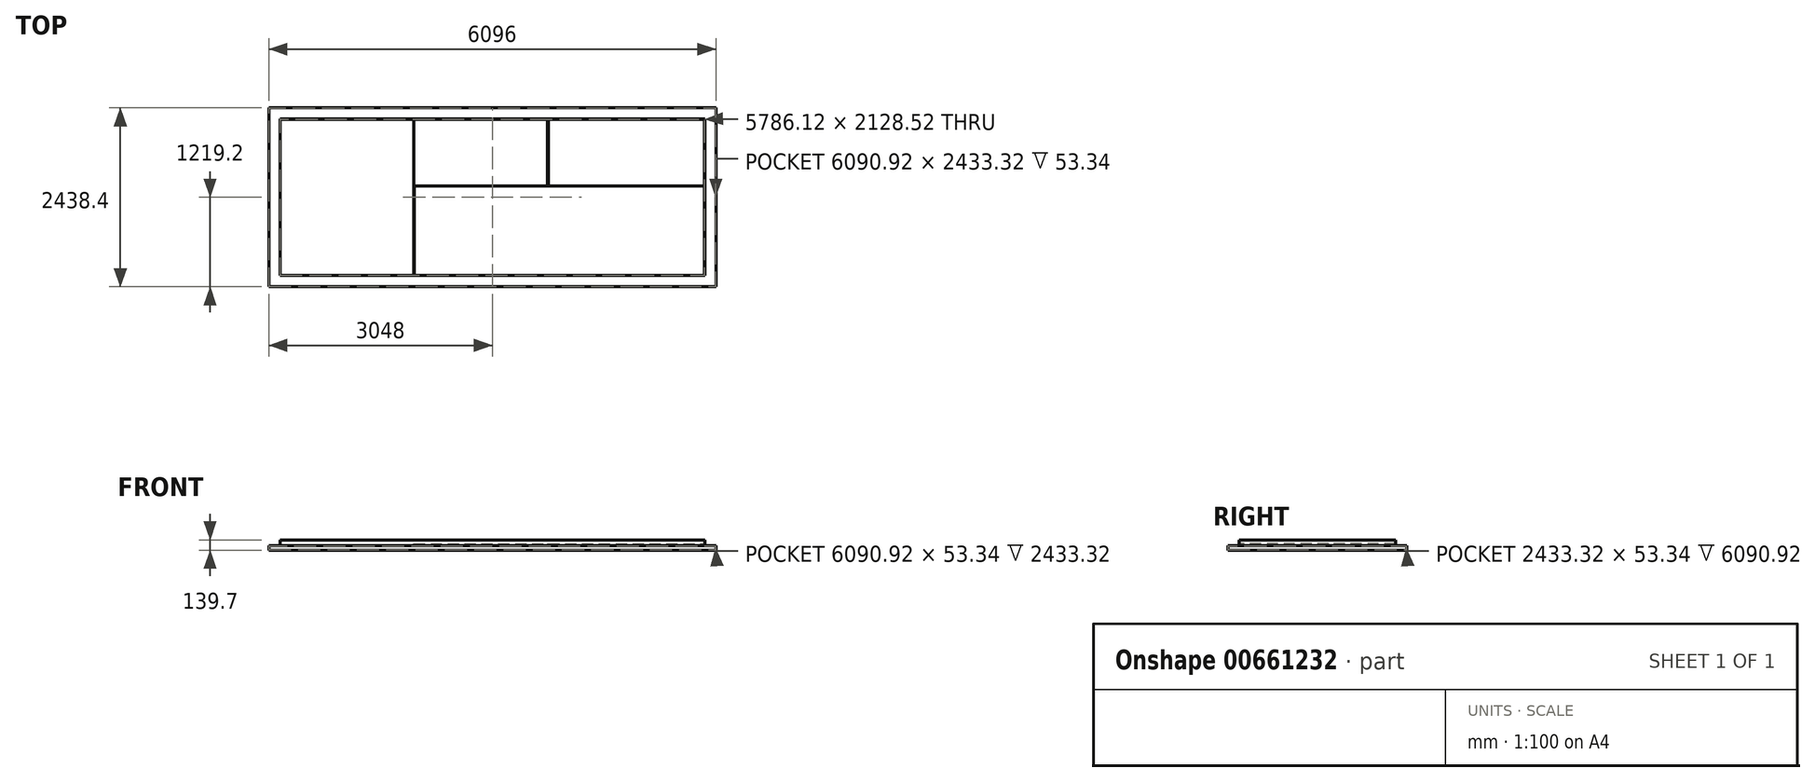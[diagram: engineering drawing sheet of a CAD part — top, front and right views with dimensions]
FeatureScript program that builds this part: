
annotation { "Feature Type Name" : "Feature", "Feature Type Description" : "" }
export const myFeature = defineFeature(function(context is Context, id is Id, definition is map)
    precondition{}
    {
        {
            var Q0;
            Q0=qCreatedBy(makeId("Top.planeOp"),FACE);
            var sketch = newSketch(context, id + "F0", { "sketchPlane" : qUnion([Q0])});
            skLineSegment(sketch, "E0.bottom", {"start": v(3048, 1219.2) * mm, "end": v(-3048, 1219.2) * mm});
            skLineSegment(sketch, "E0.top", {"start": v(3048, -1219.2) * mm, "end": v(-3048, -1219.2) * mm});
            skLineSegment(sketch, "E0.left", {"start": v(3048, 1219.2) * mm, "end": v(3048, -1219.2) * mm});
            skLineSegment(sketch, "E0.right", {"start": v(-3048, 1219.2) * mm, "end": v(-3048, -1219.2) * mm});
            skPoint(sketch, "E0.middle", {"position": v(0, 0) * mm});
            skSolve(sketch);
        }
        {
            var Q0;
            Q0=makeQuery(id+"F0.imprint","IMPRINT",FACE,{"disambiguationData":[TD([[makeQuery(id+"F0.imprint","IMPRINT",EDGE,{"derivedFrom":sQuery(id+"F0.wireOp",EDGE,"E0.bottom")}),1.0]])]});
            extrude(context, id + "F1", {"entities" : qUnion([Q0]), "depth" : 58.42 * mm, "offsetDistance" : 25.4 * mm});
        }
        {
            var Q0;
            Q0=makeQuery(id+"F1.opExtrude","CAP_FACE",FACE,{"disambiguationData":[OSD([sQuery(id+"F0.wireOp",EDGE,"E0.bottom"),sQuery(id+"F0.wireOp",EDGE,"E0.top"),sQuery(id+"F0.wireOp",EDGE,"E0.left"),sQuery(id+"F0.wireOp",EDGE,"E0.right")])],"isStart":false});
            var sketch = newSketch(context, id + "F2", { "sketchPlane" : qUnion([Q0])});
            skLineSegment(sketch, "E1.bottom", {"start": v(-2895.6, 1066.8) * mm, "end": v(2895.6, 1066.8) * mm});
            skLineSegment(sketch, "E1.top", {"start": v(-2895.6, -1066.8) * mm, "end": v(2895.6, -1066.8) * mm});
            skLineSegment(sketch, "E1.left", {"start": v(-2895.6, 1066.8) * mm, "end": v(-2895.6, -1066.8) * mm});
            skLineSegment(sketch, "E1.right", {"start": v(2895.6, 1066.8) * mm, "end": v(2895.6, -1066.8) * mm});
            skPoint(sketch, "E1.middle", {"position": v(0, 0) * mm});
            skSolve(sketch);
        }
        {
            var Q0;
            Q0=makeQuery(id+"F2.imprint","IMPRINT",FACE,{"disambiguationData":[TD([[makeQuery(id+"F2.imprint","IMPRINT",EDGE,{"derivedFrom":sQuery(id+"F2.wireOp",EDGE,"E1.bottom")}),-1.0]])]});
            extrude(context, id + "F3", {"entities" : qUnion([Q0]), "operationType" : NewBodyOperationType.ADD, "depth" : 81.28 * mm, "offsetDistance" : 25.4 * mm});
        }
        {
            var Q0;
            Q0=makeQuery(id+"F3.opExtrude","CAP_FACE",FACE,{"disambiguationData":[OSD([sQuery(id+"F2.wireOp",EDGE,"E1.bottom"),sQuery(id+"F2.wireOp",EDGE,"E1.top"),sQuery(id+"F2.wireOp",EDGE,"E1.left"),sQuery(id+"F2.wireOp",EDGE,"E1.right")])],"isStart":false});
            shell(context, id + "F4", {"entities" : qUnion([Q0]), "thickness" : 2.54 * mm});
        }
        {
            var Q0;
            Q0=makeQuery(id+"F1.opExtrude","CAP_FACE",FACE,{"disambiguationData":[OSD([sQuery(id+"F0.wireOp",EDGE,"E0.bottom"),sQuery(id+"F0.wireOp",EDGE,"E0.top"),sQuery(id+"F0.wireOp",EDGE,"E0.left"),sQuery(id+"F0.wireOp",EDGE,"E0.right")])],"isStart":false});
            var sketch = newSketch(context, id + "F5", { "sketchPlane" : qUnion([Q0])});
            skLineSegment(sketch, "E2.bottom", {"start": v(-2895.6, 1066.8) * mm, "end": v(-1066.8, 1066.8) * mm});
            skLineSegment(sketch, "E2.top", {"start": v(-2895.6, -1066.8) * mm, "end": v(-1066.8, -1066.8) * mm});
            skLineSegment(sketch, "E2.left", {"start": v(-2895.6, 1066.8) * mm, "end": v(-2895.6, -1066.8) * mm});
            skLineSegment(sketch, "E2.right", {"start": v(-1066.8, 1066.8) * mm, "end": v(-1066.8, -1066.8) * mm});
            skSolve(sketch);
        }
        {
            var Q0;
            Q0=makeQuery(id+"F5.imprint","IMPRINT",FACE,{"disambiguationData":[TD([[makeQuery(id+"F5.imprint","IMPRINT",EDGE,{"derivedFrom":sQuery(id+"F5.wireOp",EDGE,"E2.bottom")}),-1.0]])]});
            extrude(context, id + "F6", {"entities" : qUnion([Q0]), "operationType" : NewBodyOperationType.ADD, "depth" : 25.4 * mm, "offsetDistance" : 25.4 * mm});
        }
        {
            var Q0;
            Q0=makeQuery(id+"F6.opExtrude","CAP_FACE",FACE,{"disambiguationData":[OSD([sQuery(id+"F5.wireOp",EDGE,"E2.bottom"),sQuery(id+"F5.wireOp",EDGE,"E2.top"),sQuery(id+"F5.wireOp",EDGE,"E2.left"),sQuery(id+"F5.wireOp",EDGE,"E2.right")])],"isStart":false});
            shell(context, id + "F7", {"entities" : qUnion([Q0]), "thickness" : 2.54 * mm});
        }
        {
            var Q0;
            Q0=makeQuery(id+"F1.opExtrude","CAP_FACE",FACE,{"disambiguationData":[OSD([sQuery(id+"F0.wireOp",EDGE,"E0.bottom"),sQuery(id+"F0.wireOp",EDGE,"E0.top"),sQuery(id+"F0.wireOp",EDGE,"E0.left"),sQuery(id+"F0.wireOp",EDGE,"E0.right")])],"isStart":false});
            var sketch = newSketch(context, id + "F8", { "sketchPlane" : qUnion([Q0])});
            skLineSegment(sketch, "E3.bottom", {"start": v(-1071.4, 1066.8) * mm, "end": v(757.4, 1066.8) * mm});
            skLineSegment(sketch, "E3.top", {"start": v(-1071.4, 152.4) * mm, "end": v(757.4, 152.4) * mm});
            skLineSegment(sketch, "E3.left", {"start": v(-1071.4, 1066.8) * mm, "end": v(-1071.4, 152.4) * mm});
            skLineSegment(sketch, "E3.right", {"start": v(757.4, 1066.8) * mm, "end": v(757.4, 152.4) * mm});
            skSolve(sketch);
        }
        {
            var Q0;
            Q0=makeQuery(id+"F8.imprint","IMPRINT",FACE,{"disambiguationData":[TD([[makeQuery(id+"F8.imprint","IMPRINT",EDGE,{"derivedFrom":sQuery(id+"F8.wireOp",EDGE,"E3.bottom")}),-1.0]])]});
            extrude(context, id + "F9", {"entities" : qUnion([Q0]), "operationType" : NewBodyOperationType.ADD, "depth" : 25.4 * mm, "offsetDistance" : 25.4 * mm});
        }
        {
            var Q0;
            Q0=makeQuery(id+"F9.boolean.opBoolean","MERGE",FACE,{"derivedFrom":[makeQuery(id+"F6.opExtrude","CAP_FACE",FACE,{"disambiguationData":[OSD([sQuery(id+"F5.wireOp",EDGE,"E2.bottom"),sQuery(id+"F5.wireOp",EDGE,"E2.top"),sQuery(id+"F5.wireOp",EDGE,"E2.left"),sQuery(id+"F5.wireOp",EDGE,"E2.right")])],"isStart":false}),makeQuery(id+"F9.opExtrude","CAP_FACE",FACE,{"disambiguationData":[OSD([sQuery(id+"F8.wireOp",EDGE,"E3.bottom"),sQuery(id+"F8.wireOp",EDGE,"E3.top"),sQuery(id+"F8.wireOp",EDGE,"E3.left"),sQuery(id+"F8.wireOp",EDGE,"E3.right")])],"isStart":false})]});
            shell(context, id + "F10", {"entities" : qUnion([Q0]), "thickness" : 2.54 * mm});
        }
        {
            var Q0;
            Q0=makeQuery(id+"F1.opExtrude","CAP_FACE",FACE,{"disambiguationData":[OSD([sQuery(id+"F0.wireOp",EDGE,"E0.bottom"),sQuery(id+"F0.wireOp",EDGE,"E0.top"),sQuery(id+"F0.wireOp",EDGE,"E0.left"),sQuery(id+"F0.wireOp",EDGE,"E0.right")])],"isStart":false});
            var sketch = newSketch(context, id + "F11", { "sketchPlane" : qUnion([Q0])});
            skLineSegment(sketch, "E4.bottom", {"start": v(762.92, 1066.8) * mm, "end": v(2895.6, 1066.8) * mm});
            skLineSegment(sketch, "E4.top", {"start": v(762.92, 152.4) * mm, "end": v(2895.6, 152.4) * mm});
            skLineSegment(sketch, "E4.left", {"start": v(762.92, 1066.8) * mm, "end": v(762.92, 152.4) * mm});
            skLineSegment(sketch, "E4.right", {"start": v(2895.6, 1066.8) * mm, "end": v(2895.6, 152.4) * mm});
            skSolve(sketch);
        }
        {
            var Q0;
            Q0=makeQuery(id+"F11.imprint","IMPRINT",FACE,{"disambiguationData":[TD([[makeQuery(id+"F11.imprint","IMPRINT",EDGE,{"derivedFrom":sQuery(id+"F11.wireOp",EDGE,"E4.bottom")}),-1.0]])]});
            extrude(context, id + "F12", {"entities" : qUnion([Q0]), "operationType" : NewBodyOperationType.ADD, "depth" : 25.4 * mm, "offsetDistance" : 25.4 * mm});
        }
        {
            var Q0;
            Q0=makeQuery(id+"F12.opExtrude","CAP_FACE",FACE,{"disambiguationData":[OSD([sQuery(id+"F11.wireOp",EDGE,"E4.bottom"),sQuery(id+"F11.wireOp",EDGE,"E4.top"),sQuery(id+"F11.wireOp",EDGE,"E4.left"),sQuery(id+"F11.wireOp",EDGE,"E4.right")])],"isStart":false});
            shell(context, id + "F13", {"entities" : qUnion([Q0]), "thickness" : 2.54 * mm});
        }
    });
